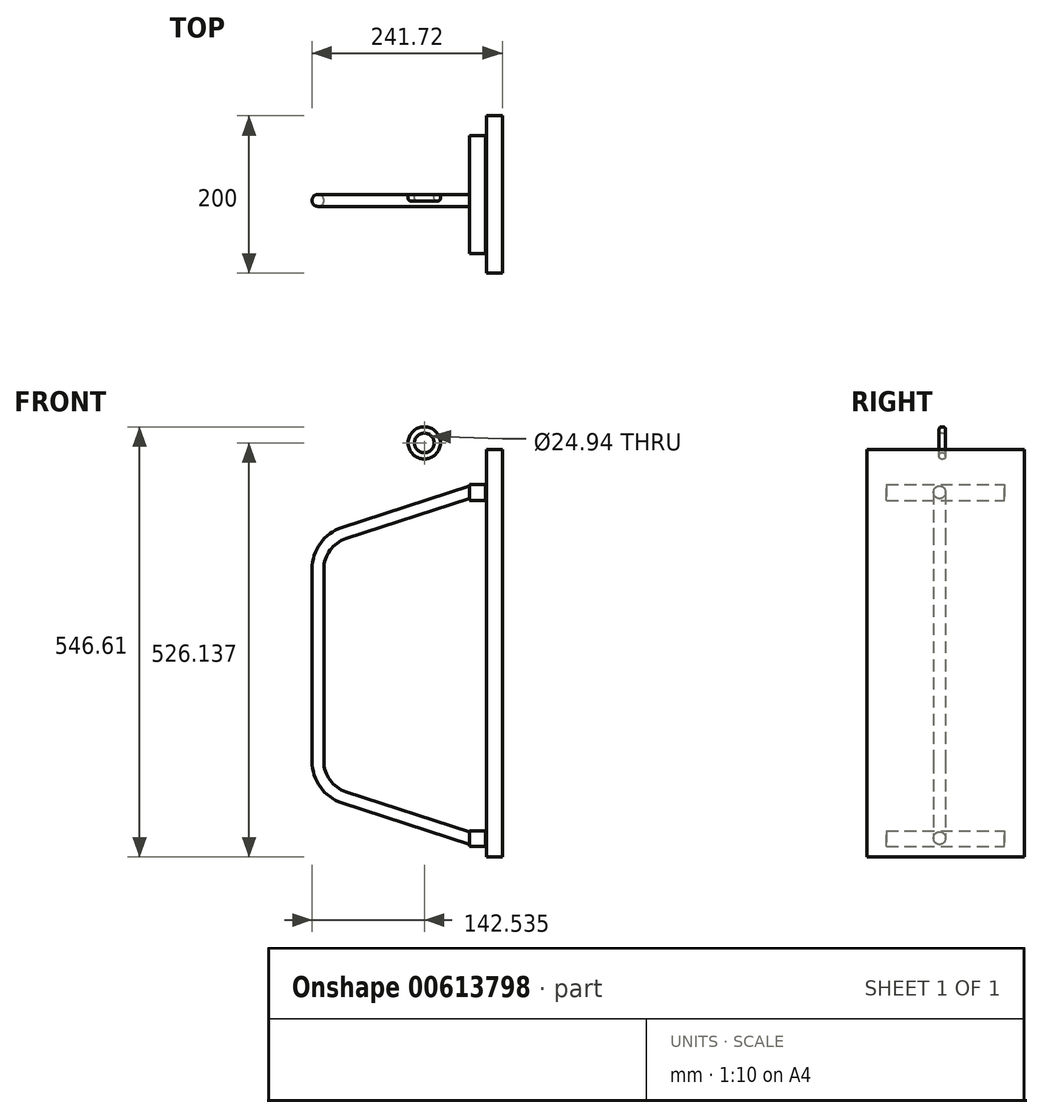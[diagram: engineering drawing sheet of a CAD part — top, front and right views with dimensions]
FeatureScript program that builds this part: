
annotation { "Feature Type Name" : "Feature", "Feature Type Description" : "" }
export const myFeature = defineFeature(function(context is Context, id is Id, definition is map)
    precondition{}
    {
        {
            var Q0;
            Q0=qCreatedBy(makeId("Front.planeOp"),FACE);
            var sketch = newSketch(context, id + "F0", { "sketchPlane" : qUnion([Q0])});
            skLineSegment(sketch, "E0.top", {"start": v(6.1, 456.9) * mm, "end": v(-13.9, 456.9) * mm});
            skLineSegment(sketch, "E0.right", {"start": v(-13.9, -2.75) * mm, "end": v(-13.9, 456.9) * mm});
            skLineSegment(sketch, "E1", {"start": v(-13.9, 455.1) * mm, "end": v(-175.58, 402.57) * mm});
            skLineSegment(sketch, "E2", {"start": v(-213.9, 349.83) * mm, "end": v(-213.9, 105.31) * mm});
            skLineSegment(sketch, "E3", {"start": v(-175.58, 52.57) * mm, "end": v(-13.9, 0.04) * mm});
            skPoint(sketch, "E4.visualSharp", {"position": v(-213.9, 390.12) * mm});
            skArc(sketch, "E4.filletArc", {"start": v(-175.58, 402.57) * mm, "mid": v(-203.3, 382.42) * mm, "end": v(-213.9, 349.83) * mm});
            skPoint(sketch, "E5.visualSharp", {"position": v(-213.9, 65.02) * mm});
            skArc(sketch, "E5.filletArc", {"start": v(-213.9, 105.31) * mm, "mid": v(-203.3, 72.72) * mm, "end": v(-175.58, 52.57) * mm});
            skLineSegment(sketch, "E6.0", {"start": v(-170.95, 66.83) * mm, "end": v(-13.9, 15.8) * mm});
            skLineSegment(sketch, "E6.1", {"start": v(-13.9, 439.33) * mm, "end": v(-170.95, 388.3) * mm});
            skArc(sketch, "E6.2", {"start": v(-170.95, 388.3) * mm, "mid": v(-191.17, 373.6) * mm, "end": v(-198.9, 349.83) * mm});
            skLineSegment(sketch, "E6.3", {"start": v(-198.9, 349.83) * mm, "end": v(-198.9, 105.31) * mm});
            skArc(sketch, "E6.4", {"start": v(-198.9, 105.31) * mm, "mid": v(-191.17, 81.53) * mm, "end": v(-170.95, 66.83) * mm});
            skLineSegment(sketch, "E7", {"start": v(6.1, 456.9) * mm, "end": v(6.1, 436.9) * mm});
            skLineSegment(sketch, "E8", {"start": v(6.1, 436.9) * mm, "end": v(6.34, 17.25) * mm, "construction": true});
            skLineSegment(sketch, "E9", {"start": v(6.34, 17.25) * mm, "end": v(6.35, -2.75) * mm});
            skLineSegment(sketch, "E10", {"start": v(6.34, 17.25) * mm, "end": v(-13.9, 17.24) * mm});
            skLineSegment(sketch, "E11", {"start": v(6.1, 436.9) * mm, "end": v(-13.9, 436.88) * mm});
            skLineSegment(sketch, "E12", {"start": v(-13.9, -2.75) * mm, "end": v(6.35, -2.75) * mm});
            skPoint(sketch, "E13.end.orphan", {"position": v(6.1, 460.49) * mm});
            skPoint(sketch, "E14.orphan", {"position": v(6.35, -3.4) * mm});
            skSolve(sketch);
        }
        {
            var Q0;
            Q0=makeQuery(id+"F0.imprint","IMPRINT",FACE,{"disambiguationData":[TD([[makeQuery(id+"F0.imprint","IMPRINT",EDGE,{"derivedFrom":sQuery(id+"F0.wireOp",EDGE,"E9")}),-1.0]])]});
            var Q1;
            {var subQ1=sQuery(id+"F0.wireOp",EDGE,"E0.top");Q1=makeQuery(id+"F0.imprint","IMPRINT",FACE,{"disambiguationData":[TD([[makeQuery(id+"F0.imprint","IMPRINT",EDGE,{"derivedFrom":subQ1}),1.0]])]});}
            extrude(context, id + "F1", {"entities" : qUnion([Q0, Q1]), "endBound" : BoundingType.SYMMETRIC, "depth" : 150 * mm, "offsetDistance" : 25 * mm});
        }
        {
            var Q0;
            {var subQ4=sQuery(id+"F0.wireOp",EDGE,"E1");Q0=makeQuery(id+"F0.imprint","IMPRINT",FACE,{"disambiguationData":[TD([[makeQuery(id+"F0.imprint","IMPRINT",EDGE,{"derivedFrom":subQ4}),1.0]])]});}
            extrude(context, id + "F2", {"entities" : qUnion([Q0]), "depth" : 15 * mm});
        }
        {
            var Q0;
            Q0=makeQuery(id+"F2.opExtrude","CAP_EDGE",EDGE,{"disambiguationData":[OSD([sQuery(id+"F0.wireOp",EDGE,"E1")])],"isStart":false});
            var Q1;
            Q1=makeQuery(id+"F2.opExtrude","CAP_EDGE",EDGE,{"disambiguationData":[OSD([sQuery(id+"F0.wireOp",EDGE,"E1")])],"isStart":true});
            var Q2;
            Q2=makeQuery(id+"F2.opExtrude","CAP_EDGE",EDGE,{"disambiguationData":[OSD([sQuery(id+"F0.wireOp",EDGE,"E6.1")])],"isStart":false});
            var Q3;
            Q3=makeQuery(id+"F2.opExtrude","CAP_EDGE",EDGE,{"disambiguationData":[OSD([sQuery(id+"F0.wireOp",EDGE,"E6.1")])],"isStart":true});
            fillet(context, id + "F3", {"entities" : qUnion([Q0, Q1, Q2, Q3]), "radius" : 7 * mm, "tangentPropagation" : true, "allowEdgeOverflow" : false});
        }
        {
            var Q0;
            Q0=qCreatedBy(makeId("Front.planeOp"),FACE);
            var sketch = newSketch(context, id + "F4", { "sketchPlane" : qUnion([Q0])});
            skCircle(sketch, "E15", {"center": v(-71.37, 509.95) * mm, "radius": 12.47 * mm});
            skCircle(sketch, "E16.0", {"center": v(-71.37, 509.95) * mm, "radius": 20.47 * mm});
            skLineSegment(sketch, "E17.0", {"start": v(4.35, -0.75) * mm, "end": v(4.34, 15.25) * mm});
            skLineSegment(sketch, "E17.1", {"start": v(-11.9, -0.75) * mm, "end": v(4.35, -0.75) * mm});
            skLineSegment(sketch, "E17.2", {"start": v(-11.9, 15.24) * mm, "end": v(-11.9, -0.75) * mm});
            skLineSegment(sketch, "E17.3", {"start": v(4.34, 15.25) * mm, "end": v(-11.9, 15.24) * mm});
            skLineSegment(sketch, "E18.top", {"start": v(7.82, 501.35) * mm, "end": v(27.82, 501.35) * mm});
            skLineSegment(sketch, "E18.left", {"start": v(7.82, -16.19) * mm, "end": v(7.82, 501.35) * mm});
            skLineSegment(sketch, "E18.right", {"start": v(27.82, -16.19) * mm, "end": v(27.82, 501.35) * mm});
            skLineSegment(sketch, "E19", {"start": v(7.82, -16.19) * mm, "end": v(27.82, -16.19) * mm});
            skSolve(sketch);
        }
        {
            var Q0;
            Q0=makeQuery(id+"F4.imprint","IMPRINT",FACE,{"disambiguationData":[TD([[makeQuery(id+"F4.imprint","IMPRINT",EDGE,{"derivedFrom":sQuery(id+"F4.wireOp",EDGE,"E15")}),-1.0]])]});
            extrude(context, id + "F5", {"entities" : qUnion([Q0]), "depth" : 8 * mm});
        }
        {
            var Q0;
            Q0=makeQuery(id+"F5.opExtrude","CAP_EDGE",EDGE,{"disambiguationData":[OSD([sQuery(id+"F4.wireOp",EDGE,"E16.0")])],"isStart":false});
            var Q1;
            Q1=makeQuery(id+"F5.opExtrude","CAP_EDGE",EDGE,{"disambiguationData":[OSD([sQuery(id+"F4.wireOp",EDGE,"E16.0")])],"isStart":true});
            var Q2;
            Q2=makeQuery(id+"F5.opExtrude","CAP_EDGE",EDGE,{"disambiguationData":[OSD([sQuery(id+"F4.wireOp",EDGE,"E15")])],"isStart":true});
            var Q3;
            Q3=makeQuery(id+"F5.opExtrude","CAP_EDGE",EDGE,{"disambiguationData":[OSD([sQuery(id+"F4.wireOp",EDGE,"E15")])],"isStart":false});
            fillet(context, id + "F6", {"entities" : qUnion([Q0, Q1, Q2, Q3]), "radius" : 3 * mm, "tangentPropagation" : true, "allowEdgeOverflow" : false});
        }
        {
            var Q0;
            {var subQ3=sQuery(id+"F4.wireOp",EDGE,"aMfKrHcZ-4CTB-L8LZ-5h8w-HNG9GgV3cerQ");Q0=makeQuery(id+"F4.imprint","IMPRINT",FACE,{"disambiguationData":[TD([[makeQuery(id+"F4.imprint","IMPRINT",EDGE,{"derivedFrom":subQ3}),-1.0]])]});}
            var Q1;
            Q1=makeQuery(id+"F4.imprint","IMPRINT",FACE,{"disambiguationData":[TD([[makeQuery(id+"F4.imprint","IMPRINT",EDGE,{"derivedFrom":sQuery(id+"F4.wireOp",EDGE,"E18.top")}),-1.0]])]});
            extrude(context, id + "F7", {"entities" : qUnion([Q0, Q1]), "endBound" : BoundingType.SYMMETRIC, "depth" : 200 * mm, "offsetDistance" : 25 * mm});
        }
    });
